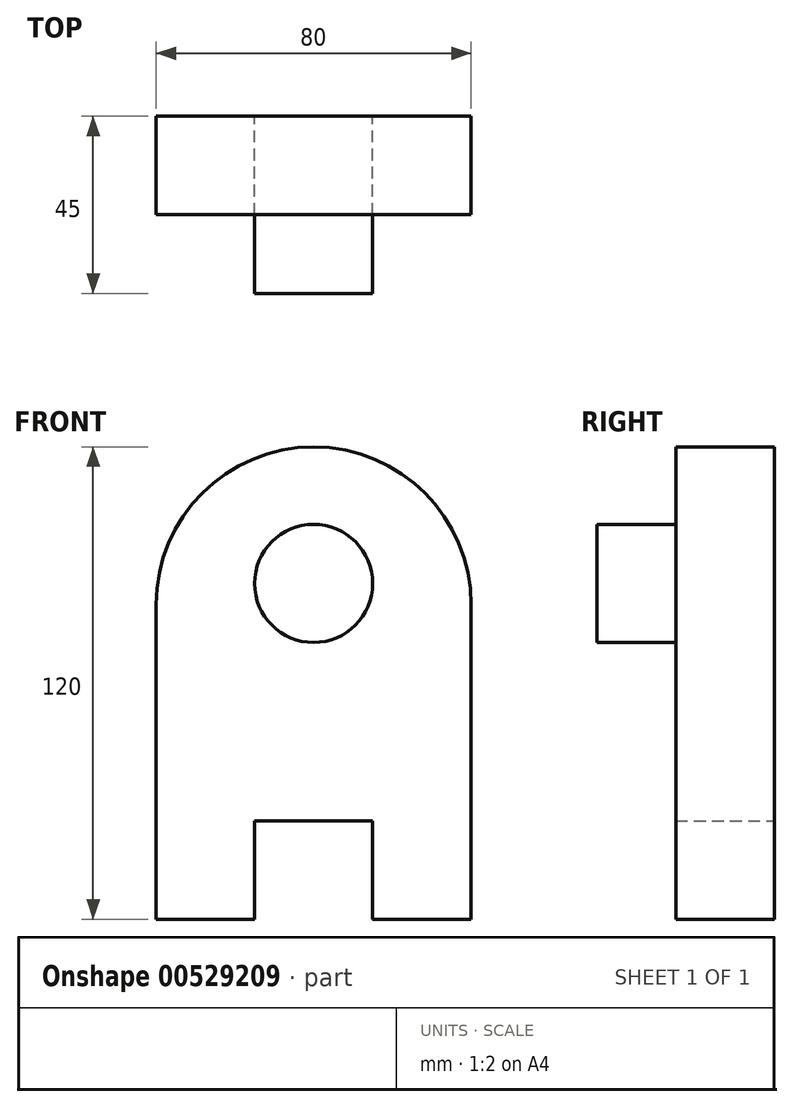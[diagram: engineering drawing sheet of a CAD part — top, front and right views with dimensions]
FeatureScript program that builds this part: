
annotation { "Feature Type Name" : "Feature", "Feature Type Description" : "" }
export const myFeature = defineFeature(function(context is Context, id is Id, definition is map)
    precondition{}
    {
        {
            var Q0;
            Q0=qCreatedBy(makeId("Front.planeOp"),FACE);
            var sketch = newSketch(context, id + "F0", { "sketchPlane" : qUnion([Q0])});
            skCircle(sketch, "E0", {"center": v(0, 41.1) * mm, "radius": 40 * mm});
            skLineSegment(sketch, "E1", {"start": v(0, 41.1) * mm, "end": v(40, 41.1) * mm});
            skLineSegment(sketch, "E2", {"start": v(0, 41.1) * mm, "end": v(-40, 41.1) * mm});
            skLineSegment(sketch, "E3", {"start": v(-40, 41.1) * mm, "end": v(-40, -38.9) * mm});
            skLineSegment(sketch, "E4", {"start": v(40, 41.1) * mm, "end": v(40, -38.9) * mm});
            skLineSegment(sketch, "E5", {"start": v(-40, -38.9) * mm, "end": v(-15, -38.9) * mm});
            skLineSegment(sketch, "E6", {"start": v(40, -38.9) * mm, "end": v(15, -38.9) * mm});
            skLineSegment(sketch, "E7", {"start": v(-15, -38.9) * mm, "end": v(-15, -13.9) * mm});
            skLineSegment(sketch, "E8", {"start": v(15, -38.9) * mm, "end": v(15, -13.9) * mm});
            skLineSegment(sketch, "E9", {"start": v(-15, -13.9) * mm, "end": v(15, -13.9) * mm});
            skSolve(sketch);
        }
        {
            var Q0;
            {var subQ0=sQuery(id+"F0.wireOp",EDGE,"E1");Q0=makeQuery(id+"F0.imprint","IMPRINT",FACE,{"disambiguationData":[TD([[makeQuery(id+"F0.imprint","IMPRINT",EDGE,{"derivedFrom":subQ0}),1.0]])]});}
            var Q1;
            {var subQ0=sQuery(id+"F0.wireOp",EDGE,"E1");Q1=makeQuery(id+"F0.imprint","IMPRINT",FACE,{"disambiguationData":[TD([[makeQuery(id+"F0.imprint","IMPRINT",EDGE,{"derivedFrom":subQ0}),-1.0]])]});}
            var Q2;
            {var subQ1=sQuery(id+"F0.wireOp",EDGE,"E3");Q2=makeQuery(id+"F0.imprint","IMPRINT",FACE,{"disambiguationData":[TD([[makeQuery(id+"F0.imprint","IMPRINT",EDGE,{"derivedFrom":subQ1}),1.0]])]});}
            extrude(context, id + "F1", {"entities" : qUnion([Q0, Q1, Q2]), "depth" : 25 * mm, "offsetDistance" : 25 * mm});
        }
        {
            var Q0;
            Q0=makeQuery(id+"F1.opExtrude","CAP_FACE",FACE,{"disambiguationData":[OSD([sQuery(id+"F0.wireOp",EDGE,"E0"),sQuery(id+"F0.wireOp",EDGE,"E3"),sQuery(id+"F0.wireOp",EDGE,"E4"),sQuery(id+"F0.wireOp",EDGE,"E5"),sQuery(id+"F0.wireOp",EDGE,"E6"),sQuery(id+"F0.wireOp",EDGE,"E7"),sQuery(id+"F0.wireOp",EDGE,"E8"),sQuery(id+"F0.wireOp",EDGE,"E9")])],"isStart":false});
            var sketch = newSketch(context, id + "F2", { "sketchPlane" : qUnion([Q0])});
            skSolve(sketch);
        }
        {
            var Q0;
            Q0=makeQuery(id+"F2.imprint","IMPRINT",FACE,{"disambiguationData":[TD([[makeQuery(id+"F2.imprint","IMPRINT",EDGE,{"derivedFrom":makeQuery(id+"F1.opExtrude","CAP_EDGE",EDGE,{"disambiguationData":[OSD([sQuery(id+"F0.wireOp",EDGE,"E0")])],"isStart":false})}),1.0]])]});
            var sketch = newSketch(context, id + "F3", { "sketchPlane" : qUnion([Q0])});
            skLineSegment(sketch, "E10", {"start": v(0, -13.6) * mm, "end": v(0, 46.4) * mm});
            skCircle(sketch, "E11", {"center": v(0, 46.4) * mm, "radius": 15 * mm});
            skSolve(sketch);
        }
        {
            var Q0;
            Q0 = qSketchRegion(id + "F3", true);
            extrude(context, id + "F4", {"entities" : qUnion([Q0]), "operationType" : NewBodyOperationType.ADD, "depth" : 20 * mm, "offsetDistance" : 25 * mm});
        }
    });
